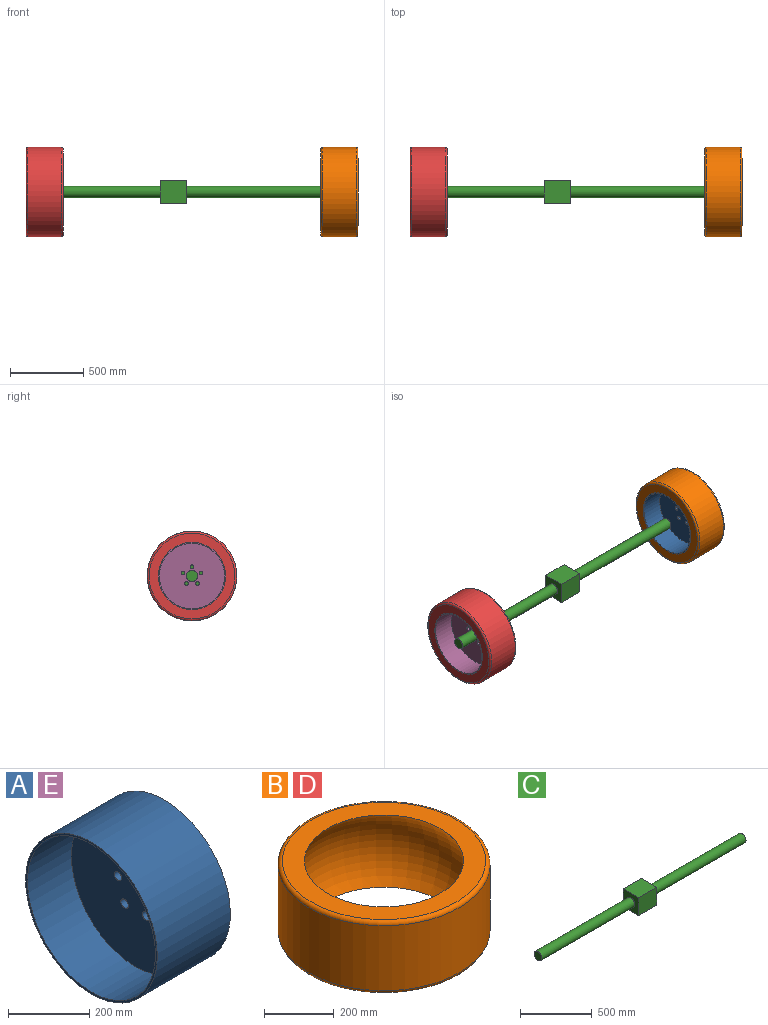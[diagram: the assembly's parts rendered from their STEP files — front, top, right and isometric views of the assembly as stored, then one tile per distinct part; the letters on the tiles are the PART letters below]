
ASSEMBLY  parts=5 mates=4
PART A: 12 faces, bbox 254x457.2x457.2 mm
  f0: cylinder r=12.7mm len=25.4mm, axis (1,0,0), area 2026.8mm2, adj f9,f11
  f1: cylinder r=12.7mm len=25.4mm, axis (1,0,0), area 2026.8mm2, adj f9,f11
  f2: cylinder r=12.7mm len=25.4mm, axis (1,0,0), area 2026.8mm2, adj f9,f11
  f3: cylinder r=12.7mm len=25.4mm, axis (1,0,0), area 2026.8mm2, adj f9,f11
  f4: cylinder r=12.7mm len=25.4mm, axis (1,0,0), area 2026.8mm2, adj f9,f11
  f5: cylinder r=228.6mm len=457.2mm, axis (-1,0,0), area 364829.4mm2, adj f6,f7
  f6: plane 457.2x457.2mm, normal (1,0,0), area 8994.1mm2, adj f5,f8
  f7: plane 457.2x457.2mm, normal (-1,0,0), area 8994.1mm2, adj f5,f10
  f8: cylinder r=222.25mm len=444.5mm, axis (1,0,0), area 106408.6mm2, adj f6,f9
  f9: plane 444.5x444.5mm, normal (1,0,0), area 152645.6mm2, adj f0,f1,f2,f3,f4,f8
  f10: cylinder r=222.25mm len=444.5mm, axis (-1,0,0), area 212817.1mm2, adj f7,f11
  f11: plane 444.5x444.5mm, normal (-1,0,0), area 152645.6mm2, adj f0,f1,f2,f3,f4,f10
PART B: 6 faces, bbox 659.8x659.8x254 mm
  f0: cylinder r=304.8mm len=609.6mm, axis (0,0,-1), area 437795.3mm2, adj f1,f5
  f1: torus R=292.1mm, axis (0,0,-1), area 37626.4mm2, adj f0,f2
  f2: plane 584.2x584.2mm, normal (0,0,-1), area 103875mm2, adj f1,f3
  f3: torus R=81.9mm, axis (0,0,-1), area 452162.5mm2, adj f2,f4
  f4: plane 584.2x584.2mm, normal (0,0,1), area 103875mm2, adj f3,f5
  f5: torus R=292.1mm, axis (0,0,-1), area 37626.4mm2, adj f0,f4
PART C: 10 faces, bbox 2006.6x152.4x152.4 mm
  f0: plane 152.4x152.4mm, normal (1,0,0), area 18665.4mm2, adj f1,f3,f4,f5,f6
  f1: plane 177.8x152.4mm, normal (0,1,0), area 27096.7mm2, adj f0,f2,f4,f5
  f2: plane 152.4x152.4mm, normal (-1,0,0), area 18665.4mm2, adj f1,f3,f4,f5,f8
  f3: plane 177.8x152.4mm, normal (0,-1,0), area 27096.7mm2, adj f0,f2,f4,f5
  f4: plane 177.8x152.4mm, normal (0,0,1), area 27096.7mm2, adj f0,f1,f2,f3
  f5: plane 177.8x152.4mm, normal (0,0,-1), area 27096.7mm2, adj f0,f1,f2,f3
  f6: cylinder r=38.1mm len=914.4mm, axis (-1,0,0), area 218897.6mm2, adj f0,f7
  f7: plane 76.2x76.2mm, normal (1,0,0), area 4560.4mm2, adj f6
  f8: cylinder r=38.1mm len=914.4mm, axis (1,0,0), area 218897.6mm2, adj f2,f9
  f9: plane 76.2x76.2mm, normal (-1,0,0), area 4560.4mm2, adj f8
PART D: same geometry as B
PART E: same geometry as A
PLACE A t=(1003.3,0,76.2)mm
PLACE B rot(axis=(0,1,0),90deg) t=(1003.3,0,76.2)mm
PLACE C at identity fixed
PLACE D rot(axis=(0,-1,0),90deg) t=(-749.3,0,76.2)mm
PLACE E t=(-1003.3,0,76.2)mm
MATE pin_slot B.f0 <-> C.f6  axis (-1,0,0) through (1003.3,0,76.2)mm
MATE pin_slot D.f0 <-> C.f6  axis (-1,0,0) through (-1003.3,0,76.2)mm
MATE pin_slot A.f8 <-> B.f0  axis (-1,0,0) through (1155.7,0,76.2)mm
MATE pin_slot E.f8 <-> D.f0  axis (-1,0,0) through (-1003.3,0,76.2)mm
